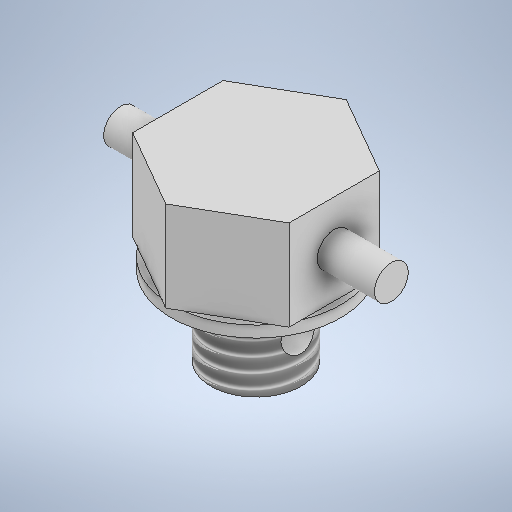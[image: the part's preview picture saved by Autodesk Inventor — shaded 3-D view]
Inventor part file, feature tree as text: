
AUTODESK INVENTOR PART (.ipt)
format: ipt  version: 2025.1 (Build 291241000, 241)  size: 304,128 bytes
history: native  units: mm
features: sketch x6, extrude x4, plane x3, hole x2, thread x1, other x1
ambient origin geometry x8: Origin, YZ Plane, XZ Plane, XY Plane, X Axis, Y Axis, Z Axis, Center Point
bodies: Solid1 (feature_tree)
feature tree (17):
  extrude  "Extrusion1"  Depth=8.0mm TaperAngle=0.0deg
  extrude  "Extrusion2"  Depth=8.0mm TaperAngle=0.0deg
  extrude  "Extrusion3"  Depth=1.0mm TaperAngle=0.0deg
  thread  "Thread1"  [1 undecoded]
  plane  "Work Plane1"
  hole  "Hole1"  [1 undecoded]
  plane  "Work Plane2"
  hole  "Hole2"  [1 undecoded]
  plane  "Work Plane3"
  extrude  "Extrusion4"  TaperAngle=0.0deg  [1 undecoded]
  sketch  "Sketch1"  dims[d0=16.0mm d1=8.0mm d2=0.0mm]
  sketch  "Sketch2"  dims[d3=8.0mm d4=8.0mm d5=0.0mm]
  sketch  "Sketch3"  dims[d6=15.0mm d7=1.0mm d8=0.0mm d9=9.5mm d10=0.0mm]
  sketch  "Sketch4"  dims[d11=7.0mm d12=4.0mm]
  sketch  "Sketch5"  dims[d13=3.0mm d14=6.0mm d15=4.0mm d16=2.0mm d17=90.0deg d18=14.0mm d19=0.0mm d20=4.0mm]
  sketch  "Sketch6"  dims[d21=3.0mm d22=3.0mm d23=6.0mm d24=4.0mm d25=2.0mm d26=90.0deg d27=8.0mm d28=0.0mm d29=0.0mm d30=24.0mm d31=0.0mm]
  other  "MS 123"
note: 4 required parameter values undecoded (feature->parameter linkage not recoverable at this tier; creation-order binding heuristic only, values carry confidence <= 0.55)
